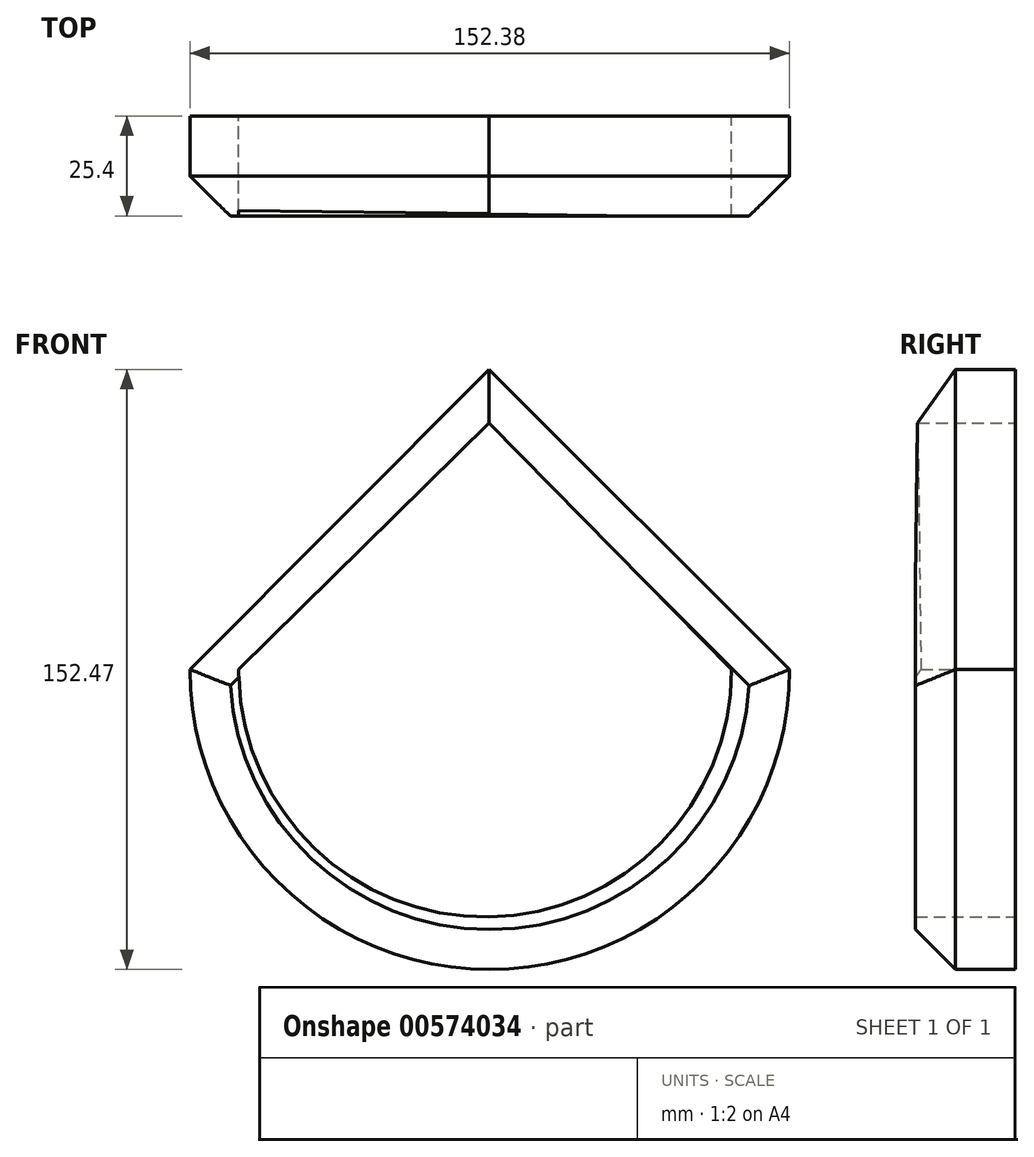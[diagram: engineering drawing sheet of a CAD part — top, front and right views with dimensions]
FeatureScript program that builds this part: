
annotation { "Feature Type Name" : "Feature", "Feature Type Description" : "" }
export const myFeature = defineFeature(function(context is Context, id is Id, definition is map)
    precondition{}
    {
        {
            var Q0;
            Q0=qCreatedBy(makeId("Front.planeOp"),FACE);
            var sketch = newSketch(context, id + "F0", { "sketchPlane" : qUnion([Q0])});
            skLineSegment(sketch, "E0", {"start": v(0, 76.19) * mm, "end": v(-75.95, 0) * mm});
            skLineSegment(sketch, "E1", {"start": v(0, 76.19) * mm, "end": v(76.43, 0) * mm});
            skArc(sketch, "E2", {"start": v(-75.95, 0) * mm, "mid": v(0.24, -76.28) * mm, "end": v(76.43, 0) * mm});
            skSolve(sketch);
        }
        {
            var Q0;
            Q0=makeQuery(id+"F0.imprint","IMPRINT",FACE,{"disambiguationData":[TD([[makeQuery(id+"F0.imprint","IMPRINT",EDGE,{"derivedFrom":sQuery(id+"F0.wireOp",EDGE,"E0")}),1.0]])]});
            extrude(context, id + "F1", {"entities" : qUnion([Q0]), "depth" : 25.4 * mm, "offsetDistance" : 25.4 * mm});
        }
        {
            var Q0;
            Q0=qCreatedBy(makeId("Front.planeOp"),FACE);
            var sketch = newSketch(context, id + "F2", { "sketchPlane" : qUnion([Q0])});
            skLineSegment(sketch, "E3", {"start": v(0, 62.57) * mm, "end": v(-63.53, 0) * mm});
            skLineSegment(sketch, "E4", {"start": v(0, 62.57) * mm, "end": v(61.63, 0) * mm});
            skArc(sketch, "E5", {"start": v(-63.53, 0) * mm, "mid": v(-0.95, -62.9) * mm, "end": v(61.63, 0) * mm});
            skSolve(sketch);
        }
        {
            var Q0;
            Q0 = qSketchRegion(id + "F2", true);
            extrude(context, id + "F3", {"entities" : qUnion([Q0]), "operationType" : NewBodyOperationType.REMOVE, "depth" : 25.4 * mm, "offsetDistance" : 25.4 * mm});
        }
        {
            var Q0;
            Q0=makeQuery(id+"F1.opExtrude","CAP_EDGE",EDGE,{"disambiguationData":[OSD([sQuery(id+"F0.wireOp",EDGE,"E0")])],"isStart":false});
            var Q1;
            Q1=makeQuery(id+"F1.opExtrude","CAP_EDGE",EDGE,{"disambiguationData":[OSD([sQuery(id+"F0.wireOp",EDGE,"E1")])],"isStart":false});
            var Q2;
            Q2=makeQuery(id+"F1.opExtrude","CAP_EDGE",EDGE,{"disambiguationData":[OSD([sQuery(id+"F0.wireOp",EDGE,"E2")])],"isStart":false});
            chamfer(context, id + "F4", {"entities" : qUnion([Q0, Q1, Q2]), "width" : 10.16 * mm, "tangentPropagation" : true});
        }
    });
